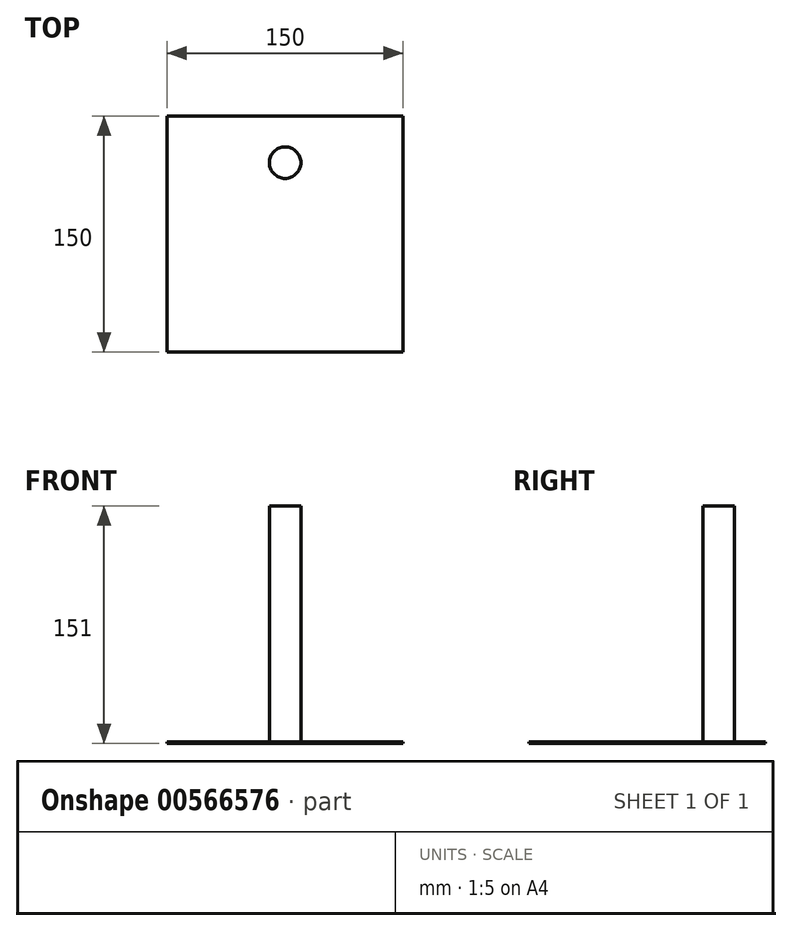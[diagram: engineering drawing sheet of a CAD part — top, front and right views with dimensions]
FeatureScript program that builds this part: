
annotation { "Feature Type Name" : "Feature", "Feature Type Description" : "" }
export const myFeature = defineFeature(function(context is Context, id is Id, definition is map)
    precondition{}
    {
        {
            var Q0;
            Q0=qCreatedBy(makeId("Top.planeOp"),FACE);
            var sketch = newSketch(context, id + "F0", { "sketchPlane" : qUnion([Q0])});
            skLineSegment(sketch, "E0.bottom", {"start": v(75, 75) * mm, "end": v(-75, 75) * mm});
            skLineSegment(sketch, "E0.top", {"start": v(75, -75) * mm, "end": v(-75, -75) * mm});
            skLineSegment(sketch, "E0.left", {"start": v(75, 75) * mm, "end": v(75, -75) * mm});
            skLineSegment(sketch, "E0.right", {"start": v(-75, 75) * mm, "end": v(-75, -75) * mm});
            skPoint(sketch, "E0.middle", {"position": v(0, 0) * mm});
            skSolve(sketch);
        }
        {
            var Q0;
            Q0=makeQuery(id+"F0.imprint","IMPRINT",FACE,{"disambiguationData":[TD([[makeQuery(id+"F0.imprint","IMPRINT",EDGE,{"derivedFrom":sQuery(id+"F0.wireOp",EDGE,"E0.bottom")}),1.0]])]});
            extrude(context, id + "F1", {"entities" : qUnion([Q0]), "oppositeDirection" : true, "depth" : 1 * mm, "offsetDistance" : 25 * mm});
        }
        {
            var Q0;
            Q0=makeQuery(id+"F1.opExtrude","CAP_FACE",FACE,{"disambiguationData":[OSD([sQuery(id+"F0.wireOp",EDGE,"E0.bottom"),sQuery(id+"F0.wireOp",EDGE,"E0.top"),sQuery(id+"F0.wireOp",EDGE,"E0.left"),sQuery(id+"F0.wireOp",EDGE,"E0.right")])],"isStart":true});
            var sketch = newSketch(context, id + "F2", { "sketchPlane" : qUnion([Q0])});
            skCircle(sketch, "E1", {"center": v(0, 45.4) * mm, "radius": 10 * mm});
            skSolve(sketch);
        }
        {
            var Q0;
            Q0=makeQuery(id+"F2.imprint","IMPRINT",FACE,{"disambiguationData":[TD([[makeQuery(id+"F2.imprint","IMPRINT",EDGE,{"derivedFrom":sQuery(id+"F2.wireOp",EDGE,"E1")}),1.0]])]});
            extrude(context, id + "F3", {"entities" : qUnion([Q0]), "operationType" : NewBodyOperationType.ADD, "depth" : 150 * mm, "offsetDistance" : 25 * mm});
        }
    });
